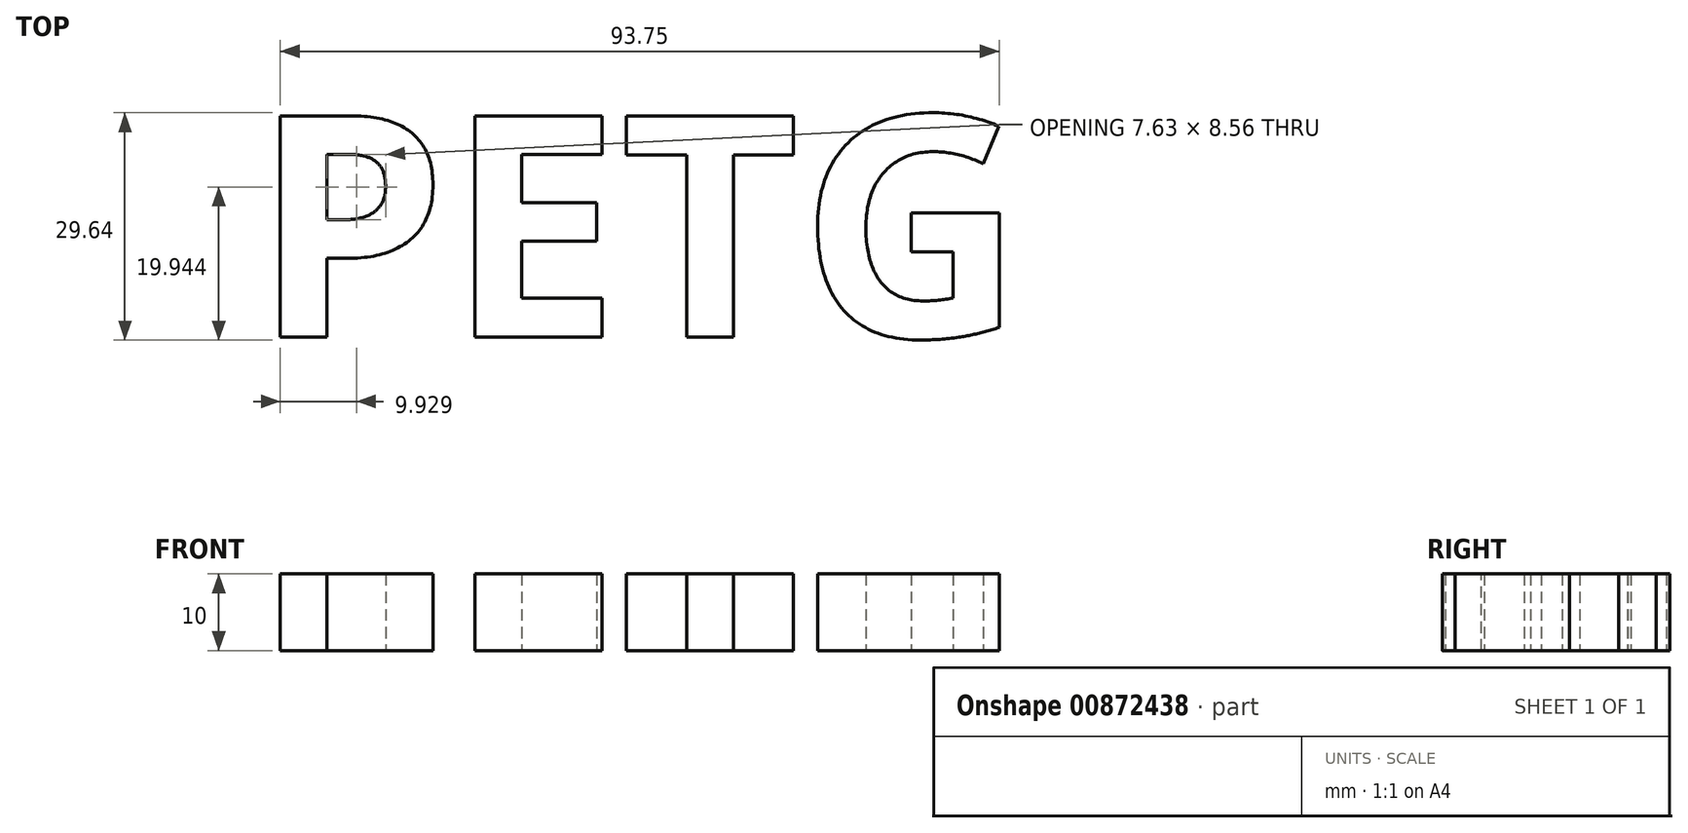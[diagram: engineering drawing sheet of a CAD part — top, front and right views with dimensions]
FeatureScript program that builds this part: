
annotation { "Feature Type Name" : "Feature", "Feature Type Description" : "" }
export const myFeature = defineFeature(function(context is Context, id is Id, definition is map)
    precondition{}
    {
        {
            var Q0;
            Q0=qCreatedBy(makeId("Top.planeOp"),FACE);
            var sketch = newSketch(context, id + "F0", { "sketchPlane" : qUnion([Q0])});
            skText(sketch, "E0", { "text": "PETG", "fontName": "OpenSans-Bold.ttf"});
            const initialGuessF0  = {"E0": [-0.05, -0.01454, 1, 0, 0.02908]};
            skSetInitialGuess(sketch, initialGuessF0);
            skSolve(sketch);
        }
        {
            var Q0;
            Q0=makeQuery(id+"F0.imprint","IMPRINT",FACE,{"disambiguationData":[TD([[makeQuery(id+"F0.imprint","IMPRINT",EDGE,{"derivedFrom":sQuery(id+"F0.wireOp",EDGE,"E0.sketch_text.stroke-0")}),-1.0]])]});
            var Q1;
            Q1=makeQuery(id+"F0.imprint","IMPRINT",FACE,{"disambiguationData":[TD([[makeQuery(id+"F0.imprint","IMPRINT",EDGE,{"derivedFrom":sQuery(id+"F0.wireOp",EDGE,"E0.sketch_text.stroke-16")}),-1.0]])]});
            var Q2;
            Q2=makeQuery(id+"F0.imprint","IMPRINT",FACE,{"disambiguationData":[TD([[makeQuery(id+"F0.imprint","IMPRINT",EDGE,{"derivedFrom":sQuery(id+"F0.wireOp",EDGE,"E0.sketch_text.stroke-28")}),-1.0]])]});
            var Q3;
            Q3=makeQuery(id+"F0.imprint","IMPRINT",FACE,{"disambiguationData":[TD([[makeQuery(id+"F0.imprint","IMPRINT",EDGE,{"derivedFrom":sQuery(id+"F0.wireOp",EDGE,"E0.sketch_text.stroke-36")}),-1.0]])]});
            extrude(context, id + "F1", {"entities" : qUnion([Q0, Q1, Q2, Q3]), "depth" : 10 * mm, "offsetDistance" : 25 * mm});
        }
    });
